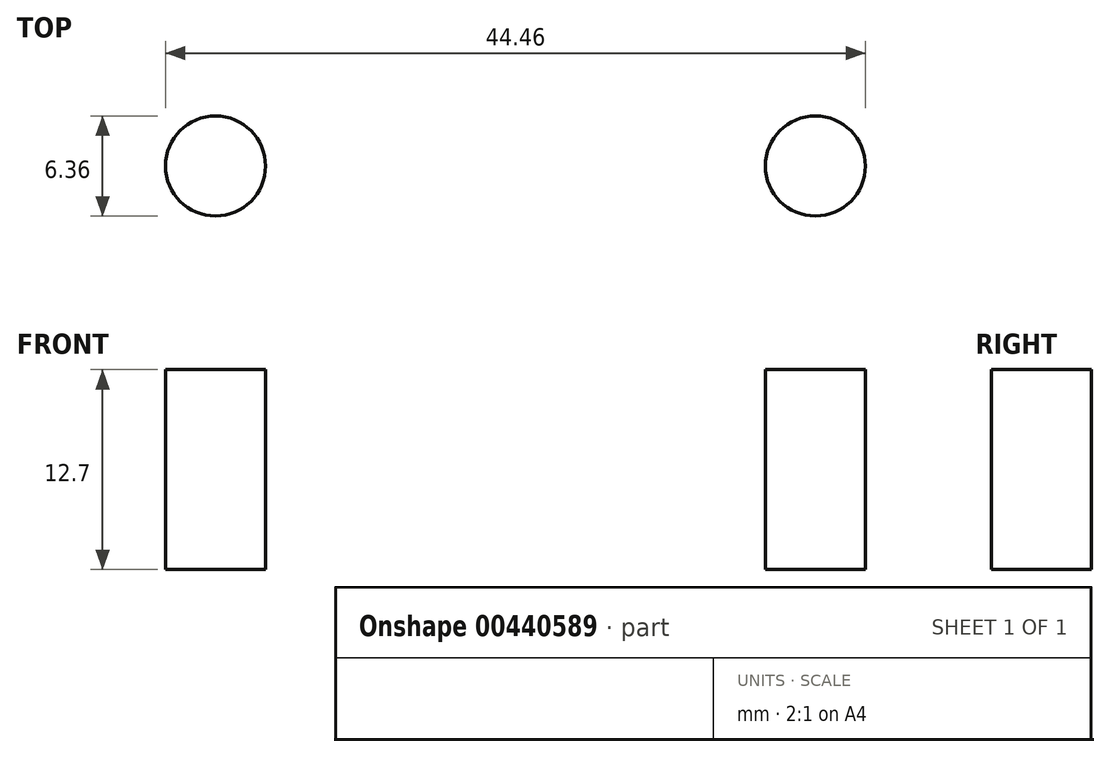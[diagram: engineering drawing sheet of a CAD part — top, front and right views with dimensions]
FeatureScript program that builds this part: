
annotation { "Feature Type Name" : "Feature", "Feature Type Description" : "" }
export const myFeature = defineFeature(function(context is Context, id is Id, definition is map)
    precondition{}
    {
        {
            var Q0;
            Q0=qCreatedBy(makeId("Top.planeOp"),FACE);
            var sketch = newSketch(context, id + "F0", { "sketchPlane" : qUnion([Q0])});
            skLineSegment(sketch, "E0.bottom", {"start": v(215.9, 25.4) * mm, "end": v(-215.9, 25.4) * mm});
            skLineSegment(sketch, "E0.top", {"start": v(215.9, -25.4) * mm, "end": v(-215.9, -25.4) * mm});
            skLineSegment(sketch, "E0.left", {"start": v(215.9, 25.4) * mm, "end": v(215.9, -25.4) * mm});
            skLineSegment(sketch, "E0.right", {"start": v(-215.9, 25.4) * mm, "end": v(-215.9, -25.4) * mm});
            skPoint(sketch, "E0.middle", {"position": v(0, 0) * mm});
            skSolve(sketch);
        }
        {
            var Q0;
            Q0 = qSketchRegion(id + "F0", true);
            extrude(context, id + "F1", {"entities" : qUnion([Q0]), "depth" : 12.7 * mm});
        }
        {
            var Q0;
            Q0=makeQuery(id+"F1.opExtrude","CAP_FACE",FACE,{"disambiguationData":[OSD([sQuery(id+"F0.wireOp",EDGE,"E0.bottom"),sQuery(id+"F0.wireOp",EDGE,"E0.top"),sQuery(id+"F0.wireOp",EDGE,"E0.left"),sQuery(id+"F0.wireOp",EDGE,"E0.right")])],"isStart":false});
            var sketch = newSketch(context, id + "F2", { "sketchPlane" : qUnion([Q0])});
            skCircle(sketch, "E1", {"center": v(12.7, 0) * mm, "radius": 12.7 * mm, "construction": true});
            skCircle(sketch, "E2", {"center": v(50.8, 0) * mm, "radius": 25.4 * mm, "construction": true});
            skCircle(sketch, "E3", {"center": v(12.7, 0) * mm, "radius": 3.18 * mm});
            skCircle(sketch, "E4", {"center": v(50.8, 0) * mm, "radius": 3.18 * mm});
            skCircle(sketch, "E5.MirrorC", {"center": v(-12.7, 0) * mm, "radius": 3.18 * mm});
            skCircle(sketch, "E6.MirrorC", {"center": v(-50.8, 0) * mm, "radius": 3.18 * mm});
            skCircle(sketch, "E7.MirrorC", {"center": v(-12.7, 0) * mm, "radius": 12.7 * mm, "construction": true});
            skCircle(sketch, "E8.MirrorC", {"center": v(-50.8, 0) * mm, "radius": 25.4 * mm, "construction": true});
            skSolve(sketch);
        }
        {
            var Q0;
            Q0=makeQuery(id+"F2.imprint","IMPRINT",FACE,{"disambiguationData":[TD([[makeQuery(id+"F2.imprint","IMPRINT",EDGE,{"derivedFrom":sQuery(id+"F2.wireOp",EDGE,"E6.MirrorC")}),-1.0]])]});
            var Q1;
            Q1=makeQuery(id+"F2.imprint","IMPRINT",FACE,{"disambiguationData":[TD([[makeQuery(id+"F2.imprint","IMPRINT",EDGE,{"derivedFrom":sQuery(id+"F2.wireOp",EDGE,"E5.MirrorC")}),-1.0]])]});
            var Q2;
            Q2=makeQuery(id+"F2.imprint","IMPRINT",FACE,{"disambiguationData":[TD([[makeQuery(id+"F2.imprint","IMPRINT",EDGE,{"derivedFrom":sQuery(id+"F2.wireOp",EDGE,"E3")}),1.0]])]});
            var Q3;
            Q3=makeQuery(id+"F2.imprint","IMPRINT",FACE,{"disambiguationData":[TD([[makeQuery(id+"F2.imprint","IMPRINT",EDGE,{"derivedFrom":sQuery(id+"F2.wireOp",EDGE,"E4")}),1.0]])]});
            extrude(context, id + "F3", {"entities" : qUnion([Q0, Q1, Q2, Q3]), "operationType" : NewBodyOperationType.REMOVE, "endBound" : BoundingType.UP_TO_NEXT, "oppositeDirection" : true, "depth" : 25.4 * mm});
        }
    });
